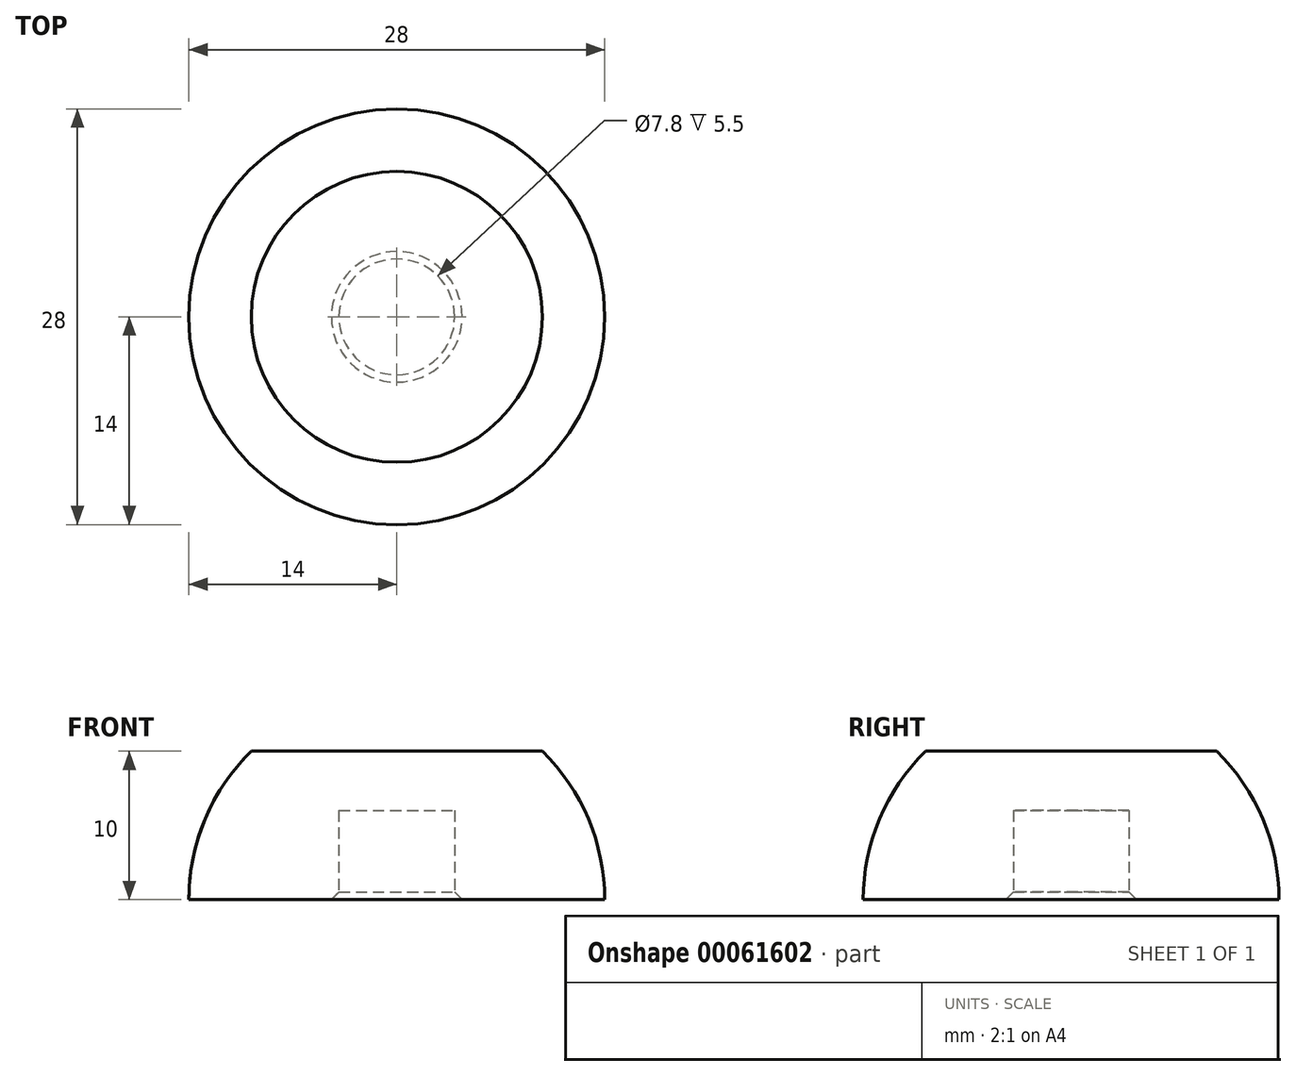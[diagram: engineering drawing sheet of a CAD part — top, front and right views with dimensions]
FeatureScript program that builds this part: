
annotation { "Feature Type Name" : "Feature", "Feature Type Description" : "" }
export const myFeature = defineFeature(function(context is Context, id is Id, definition is map)
    precondition{}
    {
        {
            var Q0;
            Q0=qCreatedBy(makeId("Front.planeOp"),FACE);
            var sketch = newSketch(context, id + "F0", { "sketchPlane" : qUnion([Q0])});
            skArc(sketch, "E0", {"start": v(-14, 0) * mm, "mid": v(-12.9, 5.42) * mm, "end": v(-9.8, 10) * mm});
            skLineSegment(sketch, "E1.bottom", {"start": v(0, 0) * mm, "end": v(-3.9, 0) * mm, "construction": true});
            skLineSegment(sketch, "E1.top", {"start": v(0, 6) * mm, "end": v(-3.9, 6) * mm, "construction": true});
            skLineSegment(sketch, "E1.left", {"start": v(0, 0) * mm, "end": v(0, 6) * mm, "construction": true});
            skLineSegment(sketch, "E1.right", {"start": v(-3.9, 0) * mm, "end": v(-3.9, 6) * mm, "construction": true});
            skLineSegment(sketch, "E2", {"start": v(-3.9, 0) * mm, "end": v(-14, 0) * mm});
            skLineSegment(sketch, "E3", {"start": v(0, 6) * mm, "end": v(0, 10) * mm});
            skLineSegment(sketch, "E4", {"start": v(0, 10) * mm, "end": v(-9.8, 10) * mm});
            skPoint(sketch, "E5.orphan", {"position": v(0, 14) * mm});
            skLineSegment(sketch, "E6", {"start": v(-3.9, 6) * mm, "end": v(-3.9, 0) * mm});
            skLineSegment(sketch, "E7", {"start": v(-3.9, 6) * mm, "end": v(0, 6) * mm});
            skSolve(sketch);
        }
        {
            var Q0;
            Q0 = qSketchRegion(id + "F0", true);
            var Q1;
            Q1=sQuery(id+"F0.wireOp",EDGE,"E3");
            revolve(context, id + "F1", {"entities" : qUnion([Q0]), "axis" : qUnion([Q1]), "revolveType" : RevolveType.FULL});
        }
        {
            var Q0;
            Q0=makeQuery(id+"F1.opRevolve","SWEPT_EDGE",EDGE,{"disambiguationData":[OSD([sQuery(id+"F0.wireOp",EDGE,"E2"),sQuery(id+"F0.wireOp",EDGE,"E6")])]});
            chamfer(context, id + "F2", {"entities" : qUnion([Q0]), "width" : 0.5 * mm});
        }
    });
